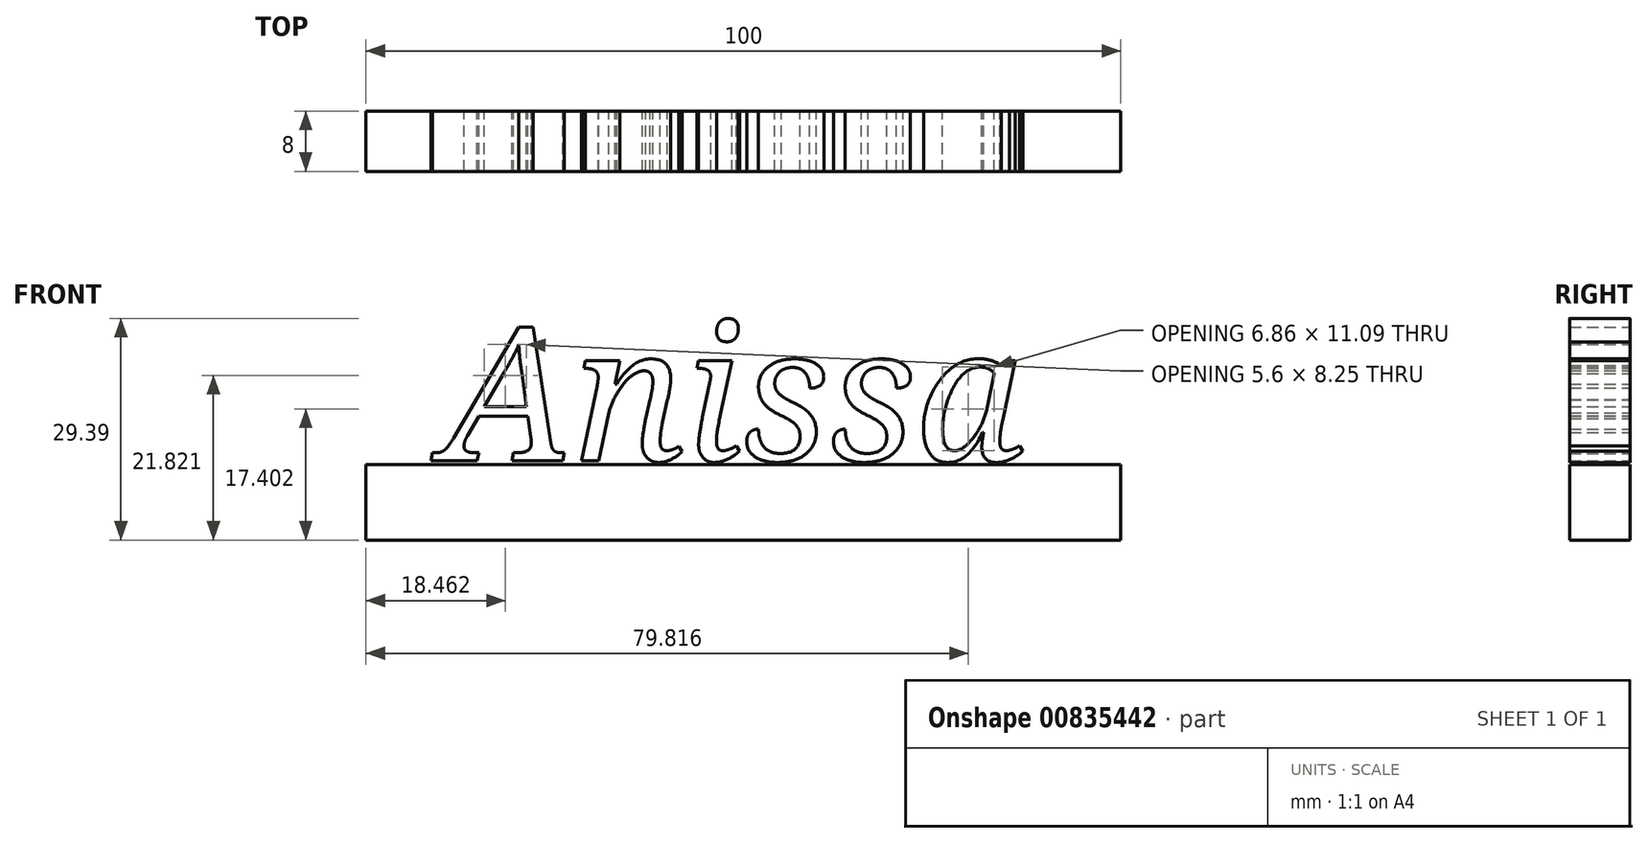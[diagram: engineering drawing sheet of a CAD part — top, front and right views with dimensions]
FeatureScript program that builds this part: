
annotation { "Feature Type Name" : "Feature", "Feature Type Description" : "" }
export const myFeature = defineFeature(function(context is Context, id is Id, definition is map)
    precondition{}
    {
        {
            var Q0;
            Q0=qCreatedBy(makeId("Front.planeOp"),FACE);
            var sketch = newSketch(context, id + "F0", { "sketchPlane" : qUnion([Q0])});
            skText(sketch, "E0", { "text": "Anissa", "fontName": "NotoSerif-Italic.ttf"});
            skLineSegment(sketch, "E1.bottom", {"start": v(-46.2, 0) * mm, "end": v(53.8, 0) * mm});
            skLineSegment(sketch, "E1.top", {"start": v(-46.2, -10) * mm, "end": v(53.8, -10) * mm});
            skLineSegment(sketch, "E1.left", {"start": v(-46.2, 0) * mm, "end": v(-46.2, -10) * mm});
            skLineSegment(sketch, "E1.right", {"start": v(53.8, 0) * mm, "end": v(53.8, -10) * mm});
            const initialGuessF0  = {"E0": [-0.0362, 0.00054, 1, 0, 0.01783]};
            skSetInitialGuess(sketch, initialGuessF0);
            skSolve(sketch);
        }
        {
            var Q0;
            Q0 = qSketchRegion(id + "F0", true);
            extrude(context, id + "F1", {"entities" : qUnion([Q0]), "flatOperationType" : FlatOperationType.REMOVE, "depth" : 8 * mm, "offsetDistance" : 25 * mm, "domain" : OperationDomain.MODEL});
        }
    });
